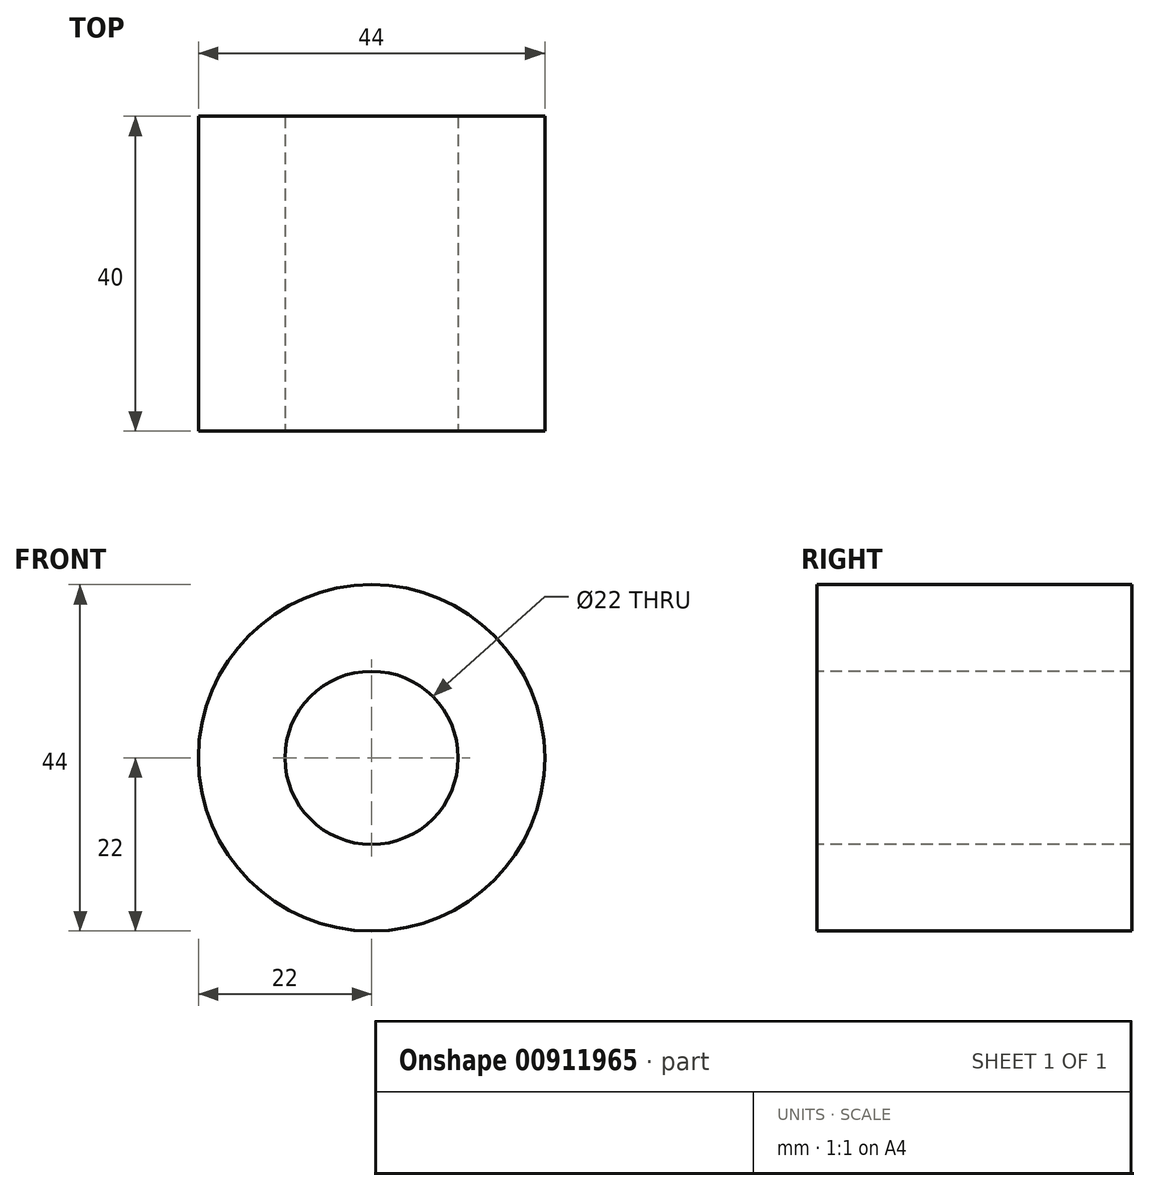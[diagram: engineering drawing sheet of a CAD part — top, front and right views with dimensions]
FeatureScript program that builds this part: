
annotation { "Feature Type Name" : "Feature", "Feature Type Description" : "" }
export const myFeature = defineFeature(function(context is Context, id is Id, definition is map)
    precondition{}
    {
        {
            var Q0;
            Q0=qCreatedBy(makeId("Front.planeOp"),FACE);
            var sketch = newSketch(context, id + "F0", { "sketchPlane" : qUnion([Q0])});
            skCircle(sketch, "E0", {"center": v(0, 0) * mm, "radius": 22 * mm});
            skCircle(sketch, "E1", {"center": v(0, 0) * mm, "radius": 11 * mm});
            skSolve(sketch);
        }
        {
            var Q0;
            Q0=makeQuery(id+"F0.imprint","IMPRINT",FACE,{"disambiguationData":[TD([[makeQuery(id+"F0.imprint","IMPRINT",EDGE,{"derivedFrom":sQuery(id+"F0.wireOp",EDGE,"E0")}),1.0]])]});
            extrude(context, id + "F1", {"entities" : qUnion([Q0]), "oppositeDirection" : true, "depth" : 40 * mm, "offsetDistance" : 25 * mm});
        }
    });
